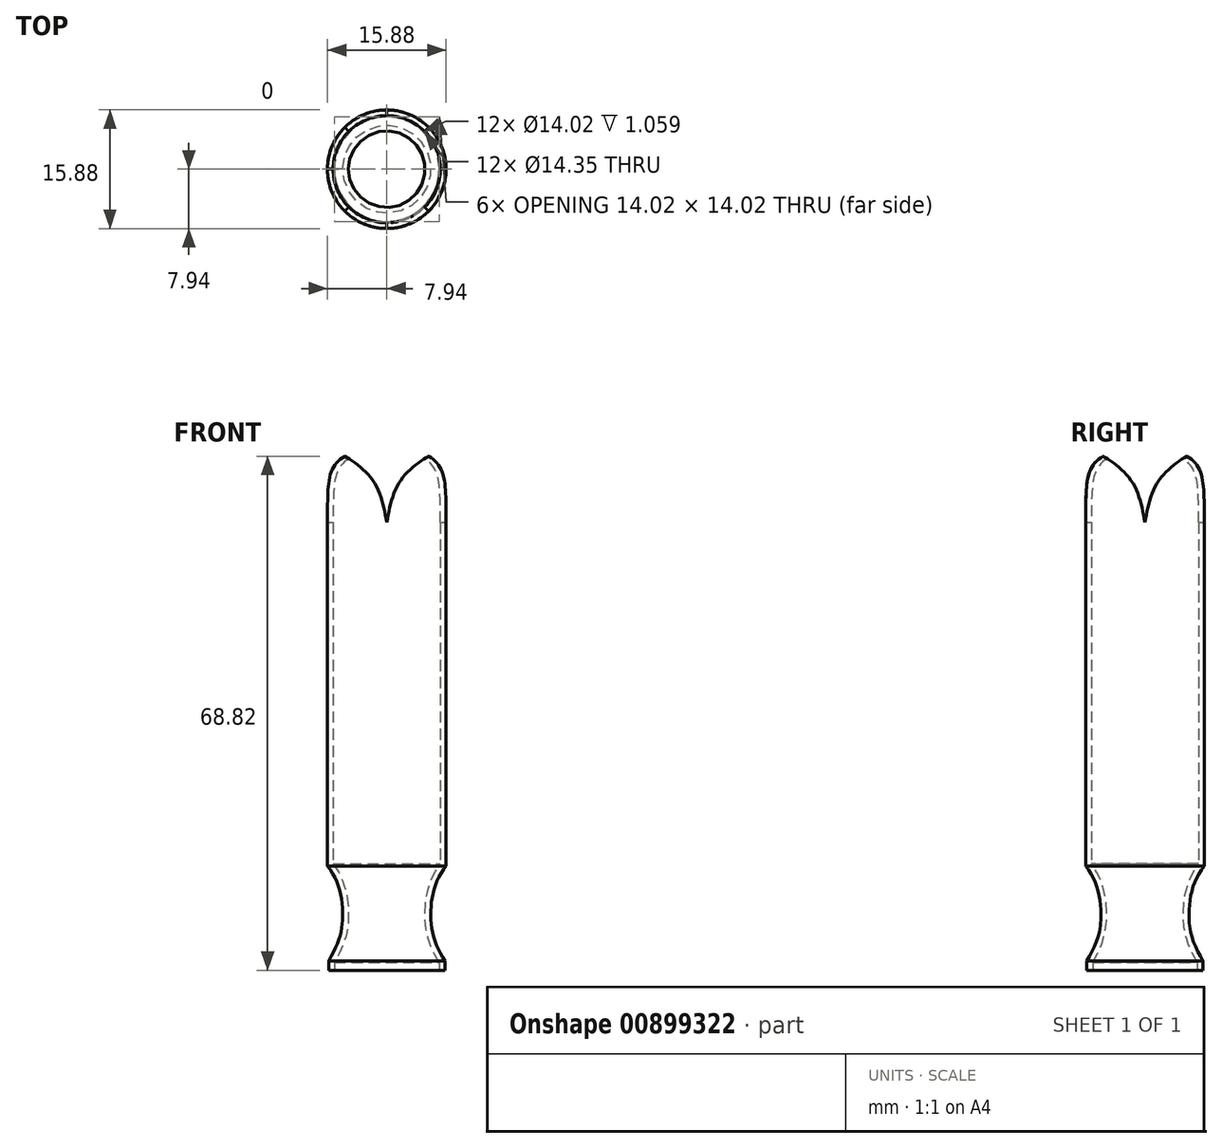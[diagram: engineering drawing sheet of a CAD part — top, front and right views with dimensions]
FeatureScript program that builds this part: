
annotation { "Feature Type Name" : "Feature", "Feature Type Description" : "" }
export const myFeature = defineFeature(function(context is Context, id is Id, definition is map)
    precondition{}
    {
        {
            var Q0;
            Q0=qCreatedBy(makeId("Front.planeOp"),FACE);
            var sketch = newSketch(context, id + "F0", { "sketchPlane" : qUnion([Q0])});
            skLineSegment(sketch, "E0", {"start": v(0, 69.85) * mm, "end": v(7.94, 69.85) * mm});
            skLineSegment(sketch, "E1", {"start": v(7.94, 69.85) * mm, "end": v(7.94, 13.97) * mm});
            skLineSegment(sketch, "E2", {"start": v(7.77, 1.27) * mm, "end": v(7.77, 0) * mm});
            skLineSegment(sketch, "E3", {"start": v(7.77, 0) * mm, "end": v(0, 0) * mm});
            skLineSegment(sketch, "E4", {"start": v(0, 0) * mm, "end": v(0, 69.85) * mm});
            skFitSpline(sketch, "E5", {"points": [v(7.94, 13.97) * mm, v(5.89, 7.44) * mm, v(7.77, 1.27) * mm], "startDerivative": vector(-9.23, -11.2) * mm, "endDerivative": vector(8.6, -14.15) * mm});
            skSolve(sketch);
        }
        {
            var Q0;
            Q0=makeQuery(id+"F0.imprint","IMPRINT",FACE,{"disambiguationData":[TD([[makeQuery(id+"F0.imprint","IMPRINT",EDGE,{"derivedFrom":sQuery(id+"F0.wireOp",EDGE,"E0")}),-1.0]])]});
            var Q1;
            Q1=sQuery(id+"F0.wireOp",EDGE,"E4");
            revolve(context, id + "F1", {"surfaceOperationType" : NewSurfaceOperationType.NEW, "entities" : qUnion([Q0]), "axis" : qUnion([Q1]), "revolveType" : RevolveType.FULL});
        }
        {
            var Q0;
            Q0=makeQuery(id+"F1.opRevolve","SWEPT_FACE",FACE,{"disambiguationData":[OSD([sQuery(id+"F0.wireOp",EDGE,"E0")])]});
            var Q1;
            Q1=makeQuery(id+"F1.opRevolve","SWEPT_FACE",FACE,{"disambiguationData":[OSD([sQuery(id+"F0.wireOp",EDGE,"E3")])]});
            shell(context, id + "F2", {"entities" : qUnion([Q0, Q1]), "thickness" : 0.76 * mm});
        }
        {
            var Q0;
            Q0=qCreatedBy(makeId("Front.planeOp"),FACE);
            var sketch = newSketch(context, id + "F3", { "sketchPlane" : qUnion([Q0])});
            skLineSegment(sketch, "E6", {"start": v(-7.94, 69.85) * mm, "end": v(7.94, 69.85) * mm});
            skFitSpline(sketch, "E7", {"points": [v(-7.94, 69.85) * mm, v(-2.17, 65.98) * mm, v(0, 59.97) * mm], "startDerivative": vector(16.87, -5.92) * mm, "endDerivative": vector(3.68, -20.31) * mm});
            skFitSpline(sketch, "E8.MirrorCS", {"points": [v(7.94, 69.85) * mm, v(2.17, 65.98) * mm, v(0, 59.97) * mm], "startDerivative": vector(-16.87, -5.92) * mm, "endDerivative": vector(-3.68, -20.31) * mm});
            skSolve(sketch);
        }
        {
            var Q0;
            Q0=makeQuery(id+"F3.imprint","IMPRINT",FACE,{"disambiguationData":[TD([[makeQuery(id+"F3.imprint","IMPRINT",EDGE,{"derivedFrom":sQuery(id+"F3.wireOp",EDGE,"E6")}),-1.0]])]});
            extrude(context, id + "F4", {"entities" : qUnion([Q0]), "endBound" : BoundingType.SYMMETRIC, "depth" : 25.4 * mm, "offsetDistance" : 25.4 * mm});
        }
        {
            var Q0;
            Q0=makeQuery(id+"F4.opExtrude","SWEPT_BODY",BODY,{"disambiguationData":[OSD([sQuery(id+"F3.wireOp",EDGE,"E6"),sQuery(id+"F3.wireOp",EDGE,"E7"),sQuery(id+"F3.wireOp",EDGE,"E8.MirrorCS")])]});
            var Q1;
            Q1=makeQuery(id+"F2.opShell","OFFSET_EDGE",EDGE,{"disambiguationData":[OSD([sQuery(id+"F0.wireOp",EDGE,"E0"),sQuery(id+"F0.wireOp",EDGE,"E1")])]});
            transform(context, id + "F5", {"entities" : qUnion([Q0]), "transformType" : TransformType.ROTATION, "transformAxis" : qUnion([Q1]), "angle" : 90 * degree, "makeCopy" : true});
        }
        {
            var Q0;
            Q0=makeQuery(id+"F5.opPattern","COPY",BODY,{"derivedFrom":makeQuery(id+"F4.opExtrude","SWEPT_BODY",BODY,{"disambiguationData":[OSD([sQuery(id+"F3.wireOp",EDGE,"E6"),sQuery(id+"F3.wireOp",EDGE,"E7"),sQuery(id+"F3.wireOp",EDGE,"E8.MirrorCS")])]}),"instanceName":"1"});
            var Q1;
            Q1=makeQuery(id+"F4.opExtrude","SWEPT_BODY",BODY,{"disambiguationData":[OSD([sQuery(id+"F3.wireOp",EDGE,"E6"),sQuery(id+"F3.wireOp",EDGE,"E7"),sQuery(id+"F3.wireOp",EDGE,"E8.MirrorCS")])]});
            var Q2;
            Q2=makeQuery(id+"F1.opRevolve","SWEPT_BODY",BODY,{"disambiguationData":[OSD([sQuery(id+"F0.wireOp",EDGE,"E0"),sQuery(id+"F0.wireOp",EDGE,"E1"),sQuery(id+"F0.wireOp",EDGE,"E2"),sQuery(id+"F0.wireOp",EDGE,"E3"),sQuery(id+"F0.wireOp",EDGE,"E4"),sQuery(id+"F0.wireOp",EDGE,"E5")])]});
            booleanBodies(context, id + "F6", {"operationType" : BooleanOperationType.SUBTRACTION, "tools" : qUnion([Q0, Q1]), "targets" : qUnion([Q2])});
        }
    });
